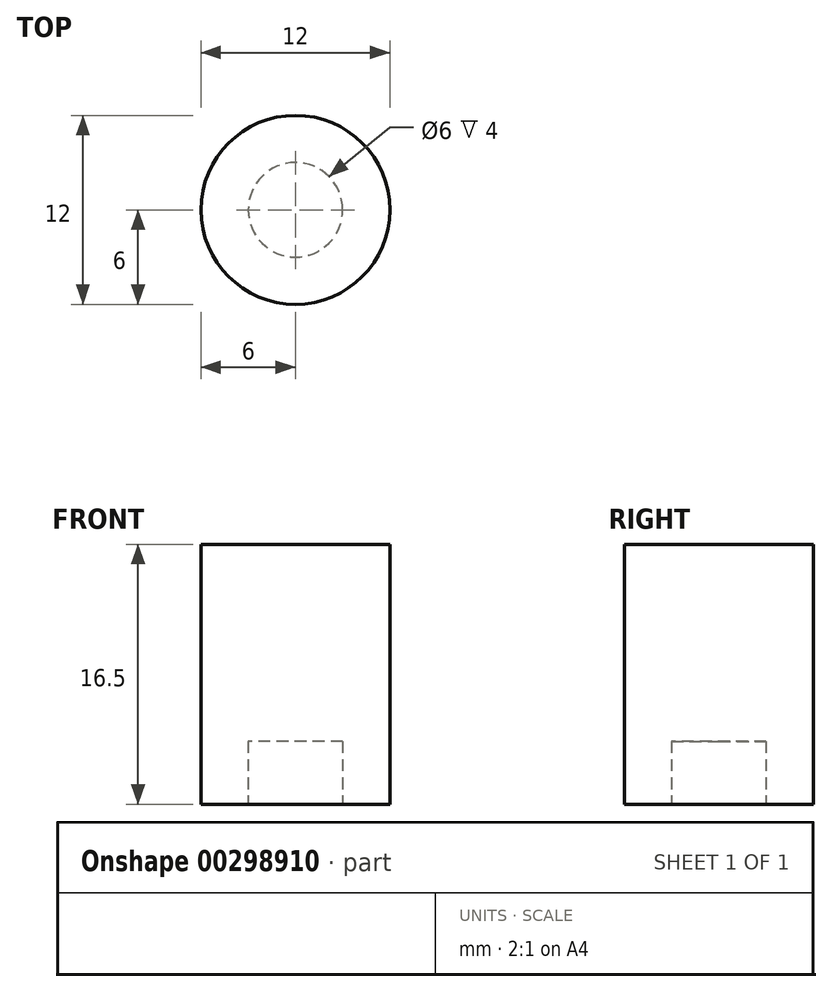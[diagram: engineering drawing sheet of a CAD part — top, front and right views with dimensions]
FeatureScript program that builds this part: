
annotation { "Feature Type Name" : "Feature", "Feature Type Description" : "" }
export const myFeature = defineFeature(function(context is Context, id is Id, definition is map)
    precondition{}
    {
        {
            var Q0;
            Q0=qCreatedBy(makeId("Top.planeOp"),FACE);
            var sketch = newSketch(context, id + "F0", { "sketchPlane" : qUnion([Q0])});
            skCircle(sketch, "E0", {"center": v(0, 0) * mm, "radius": 6 * mm});
            skSolve(sketch);
        }
        {
            var Q0;
            Q0 = qSketchRegion(id + "F0", true);
            extrude(context, id + "F1", {"entities" : qUnion([Q0]), "offsetDistance" : 25 * mm, "depth" : 16.5 * mm});
        }
        {
            var Q0;
            Q0=qCreatedBy(makeId("Top.planeOp"),FACE);
            var sketch = newSketch(context, id + "F2", { "sketchPlane" : qUnion([Q0])});
            skCircle(sketch, "E1", {"center": v(0, 0) * mm, "radius": 3 * mm});
            skSolve(sketch);
        }
        {
            var Q0;
            Q0 = qSketchRegion(id + "F2", true);
            extrude(context, id + "F3", {"entities" : qUnion([Q0]), "operationType" : NewBodyOperationType.REMOVE, "offsetDistance" : 25 * mm, "depth" : 4 * mm});
        }
    });
